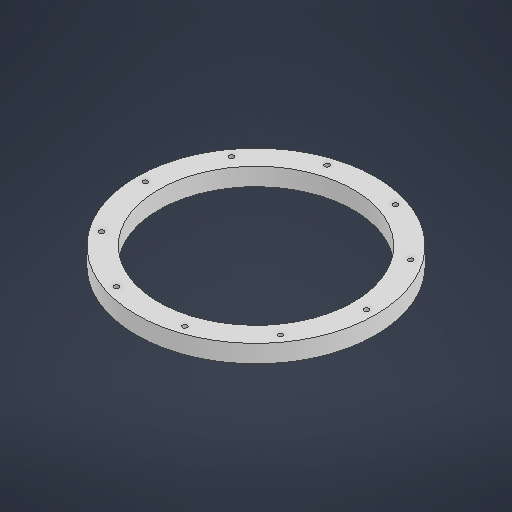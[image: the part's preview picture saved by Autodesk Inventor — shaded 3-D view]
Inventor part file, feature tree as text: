
AUTODESK INVENTOR PART (.ipt)
format: ipt  version: 2025 (Build 290162000, 162)  size: 223,744 bytes
history: native  units: in
note: dims shown in document units (in); Inventor stores cm internally (conversion verified against a paired STEP export)
features: sketch x3, extrude x1, hole x1
ambient origin geometry x8: Origin, YZ Plane, XZ Plane, XY Plane, X Axis, Y Axis, Z Axis, Center Point
bodies: Solid1 (feature_tree)
feature tree (5):
  extrude  "Extrusion1"  Depth=8.6614in
  hole  "Hole1"  [1 undecoded]
  sketch  "Sketch1"  dims[d0=10.6299in d1=8.6614in]
  sketch  "Sketch3"  dims[d8=0.1969in d9=3.937in d11=360.0deg d13=0.2165in d14=0.2362in d15=0.1575in d16=0.0787in d17=90.0deg d18=0.315in d19=0.8108in]
  sketch  "Sketch Circular Pattern1"  dims[d2=0.7874in d3=0.0in d7=9.8425in]
note: 1 required parameter value undecoded (feature->parameter linkage not recoverable at this tier; creation-order binding heuristic only, values carry confidence <= 0.55)
